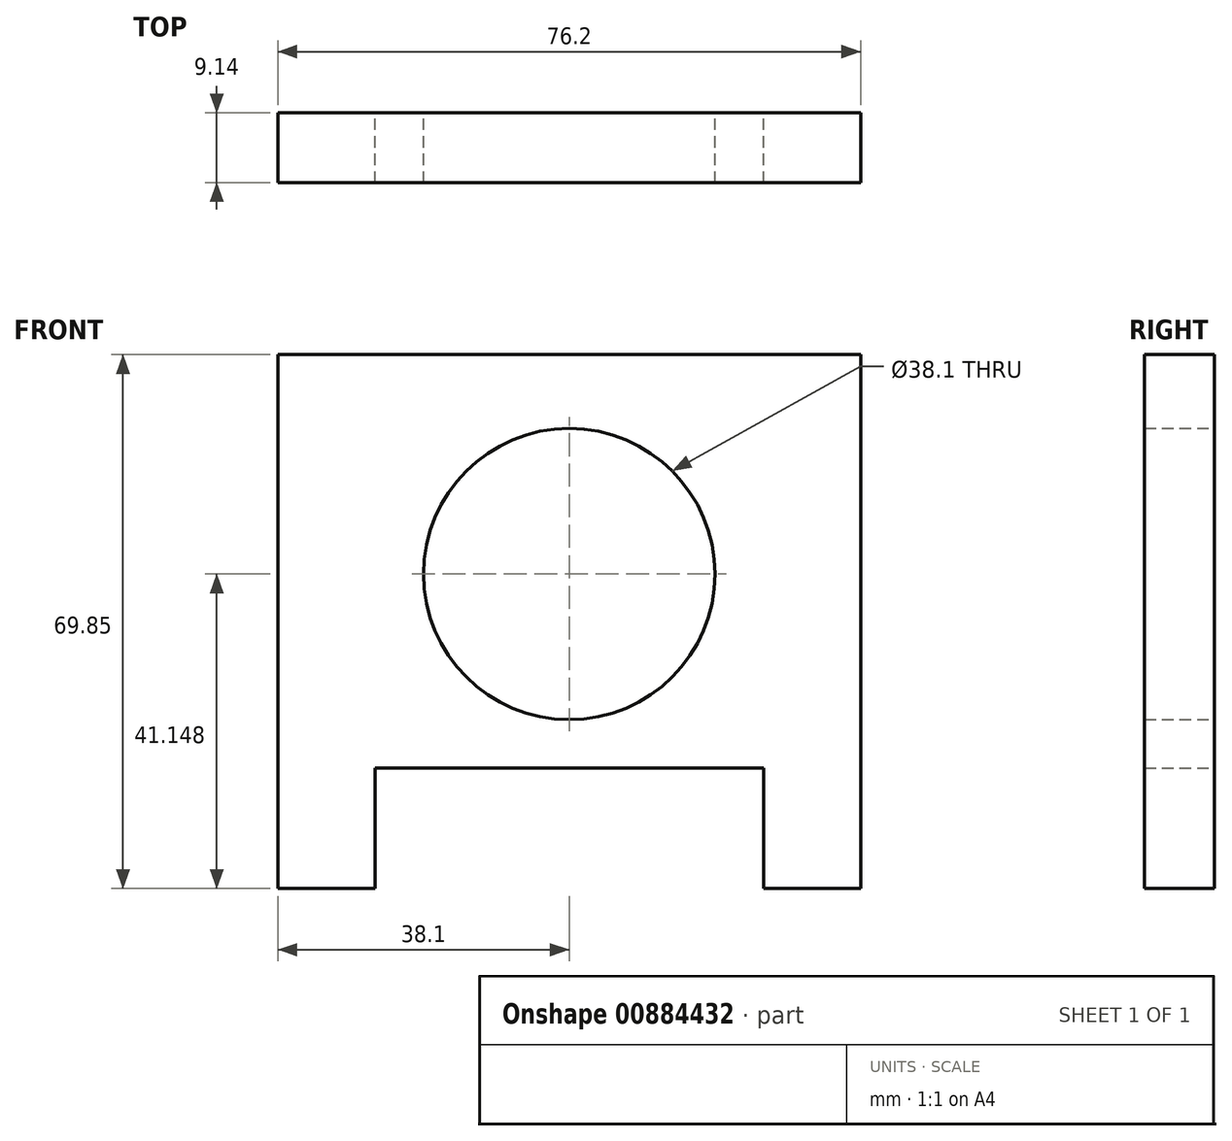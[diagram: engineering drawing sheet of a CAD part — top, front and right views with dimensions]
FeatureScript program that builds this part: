
annotation { "Feature Type Name" : "Feature", "Feature Type Description" : "" }
export const myFeature = defineFeature(function(context is Context, id is Id, definition is map)
    precondition{}
    {
        {
            var Q0;
            Q0=qCreatedBy(makeId("Front.planeOp"),FACE);
            var sketch = newSketch(context, id + "F0", { "sketchPlane" : qUnion([Q0])});
            skLineSegment(sketch, "E0.bottom", {"start": v(-38.1, 69.85) * mm, "end": v(38.1, 69.85) * mm});
            skLineSegment(sketch, "E0.top", {"start": v(-38.1, 0) * mm, "end": v(-25.4, 0) * mm});
            skLineSegment(sketch, "E0.left", {"start": v(-38.1, 69.85) * mm, "end": v(-38.1, 0) * mm});
            skLineSegment(sketch, "E0.right", {"start": v(38.1, 69.85) * mm, "end": v(38.1, 0) * mm});
            skCircle(sketch, "E1", {"center": v(0, 41.15) * mm, "radius": 19.05 * mm});
            skLineSegment(sketch, "E2", {"start": v(-25.4, 0) * mm, "end": v(-25.4, 15.75) * mm});
            skLineSegment(sketch, "E3", {"start": v(-25.4, 15.75) * mm, "end": v(25.4, 15.75) * mm});
            skLineSegment(sketch, "E4", {"start": v(25.4, 15.75) * mm, "end": v(25.4, 0) * mm});
            skLineSegment(sketch, "E5.trimOffspring", {"start": v(25.4, 0) * mm, "end": v(38.1, 0) * mm});
            skSolve(sketch);
        }
        {
            var Q0;
            Q0=makeQuery(id+"F0.imprint","IMPRINT",FACE,{"disambiguationData":[TD([[makeQuery(id+"F0.imprint","IMPRINT",EDGE,{"derivedFrom":sQuery(id+"F0.wireOp",EDGE,"E0.bottom")}),-1.0]])]});
            extrude(context, id + "F1", {"entities" : qUnion([Q0]), "depth" : 9.14 * mm, "offsetDistance" : 25.4 * mm});
        }
    });
